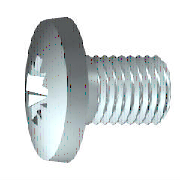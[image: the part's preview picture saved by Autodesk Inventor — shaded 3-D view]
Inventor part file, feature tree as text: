
AUTODESK INVENTOR PART (.ipt)
format: ipt  version: 2015 (Build 190159000, 159)  size: 215,552 bytes
history: native  units: mm (DEFAULTED — no unit token found)
features: other x3, chamfer x2, fillet x2, sketch x2, revolve x1, extrude x1, pattern_circular x1
ambient origin geometry x8: Origin, YZ Plane, XZ Plane, XY Plane, X Axis, Y Axis, Z Axis, Center Point
bodies: Solid1 (feature_tree)
feature tree (12):
  revolve  "Revolution1"  [1 undecoded]
  chamfer  "Chamfer1"  Distance=0.15mm
  chamfer  "Chamfer2"  Distance=0.15mm
  fillet  "Fillet1"  Radius=0.3mm
  extrude  "Extrusion1"  Depth=0.666667mm
  pattern_circular  "PolarArray1"  [2 undecoded]
  fillet  "Fillet2"  Radius=2.08mm
  other  "MSC_A1"
  other  "MSC_PF1"
  other  "MSC_PT1"
  sketch  "Sketch2"  dims[d6=3.2mm d9=0.872665mm]
  sketch  "Sketch3"  dims[d10=90.0deg d11=0.15mm d12=0.15mm d13=0.3mm d14=0.3mm d16=10.0mm d17=0.0mm d19=2.08mm d20=0.8mm d21=2.82mm d22=0.8mm d23=0.0mm d24=40.0mm d26=360.0deg d27=0.0mm d28=0.0mm d29=0.0mm d34=0.666667mm d35=45.0deg d36=45.0deg d38=0.0mm d39=0.0mm]
note: 3 required parameter values undecoded (feature->parameter linkage not recoverable at this tier; creation-order binding heuristic only, values carry confidence <= 0.55)